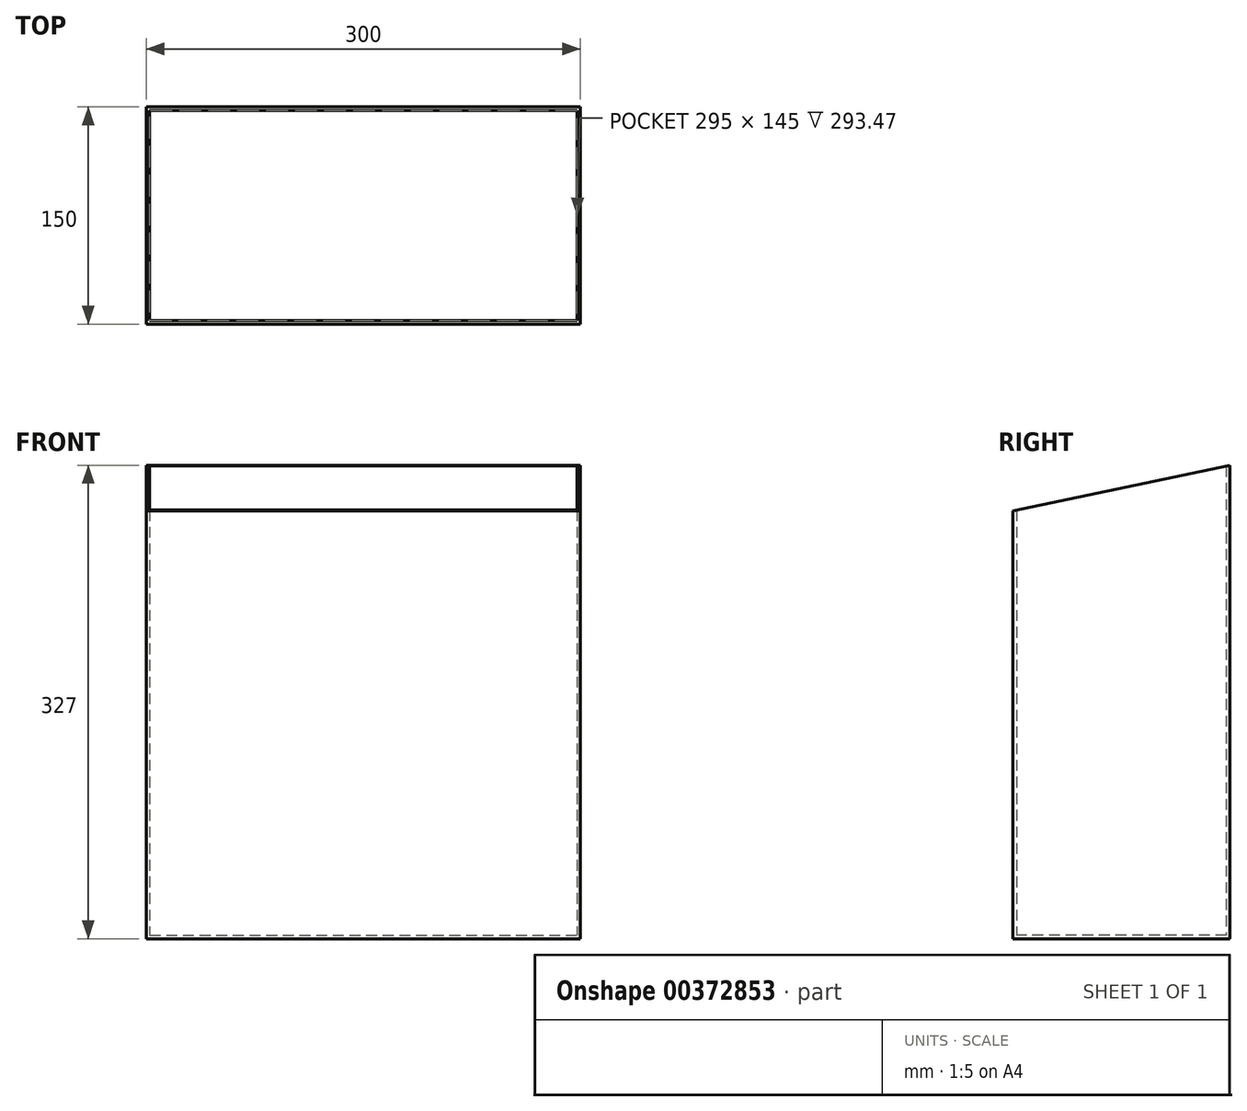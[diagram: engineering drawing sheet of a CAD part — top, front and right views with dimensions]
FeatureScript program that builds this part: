
annotation { "Feature Type Name" : "Feature", "Feature Type Description" : "" }
export const myFeature = defineFeature(function(context is Context, id is Id, definition is map)
    precondition{}
    {
        {
            var Q0;
            Q0=qCreatedBy(makeId("Top.planeOp"),FACE);
            var sketch = newSketch(context, id + "F0", { "sketchPlane" : qUnion([Q0])});
            skLineSegment(sketch, "E0", {"start": v(0, 0) * mm, "end": v(300, 0) * mm});
            skLineSegment(sketch, "E1", {"start": v(300, 0) * mm, "end": v(300, 150) * mm});
            skLineSegment(sketch, "E2", {"start": v(300, 150) * mm, "end": v(0, 150) * mm});
            skLineSegment(sketch, "E3", {"start": v(0, 150) * mm, "end": v(0, 0) * mm});
            skSolve(sketch);
        }
        {
            var Q0;
            Q0 = qSketchRegion(id + "F0", true);
            extrude(context, id + "F1", {"entities" : qUnion([Q0]), "depth" : 327 * mm});
        }
        {
            var Q0;
            Q0=makeQuery(id+"F1.opExtrude","CAP_FACE",FACE,{"disambiguationData":[OSD([sQuery(id+"F0.wireOp",EDGE,"E0"),sQuery(id+"F0.wireOp",EDGE,"E1"),sQuery(id+"F0.wireOp",EDGE,"E2"),sQuery(id+"F0.wireOp",EDGE,"E3")])],"isStart":false});
            shell(context, id + "F2", {"entities" : qUnion([Q0]), "thickness" : 2.5 * mm});
        }
        {
            var Q0;
            Q0=makeQuery(id+"F1.opExtrude","SWEPT_FACE",FACE,{"disambiguationData":[OSD([sQuery(id+"F0.wireOp",EDGE,"E1")])]});
            var sketch = newSketch(context, id + "F3", { "sketchPlane" : qUnion([Q0])});
            skLineSegment(sketch, "E4", {"start": v(150, 327) * mm, "end": v(0, 295.44) * mm});
            skLineSegment(sketch, "E5", {"start": v(0, 295.44) * mm, "end": v(0, 327) * mm});
            skLineSegment(sketch, "E6", {"start": v(0, 327) * mm, "end": v(150, 327) * mm});
            skSolve(sketch);
        }
        {
            var Q0;
            Q0 = qSketchRegion(id + "F3", true);
            extrude(context, id + "F4", {"entities" : qUnion([Q0]), "operationType" : NewBodyOperationType.REMOVE, "oppositeDirection" : true, "depth" : 346 * mm});
        }
    });
